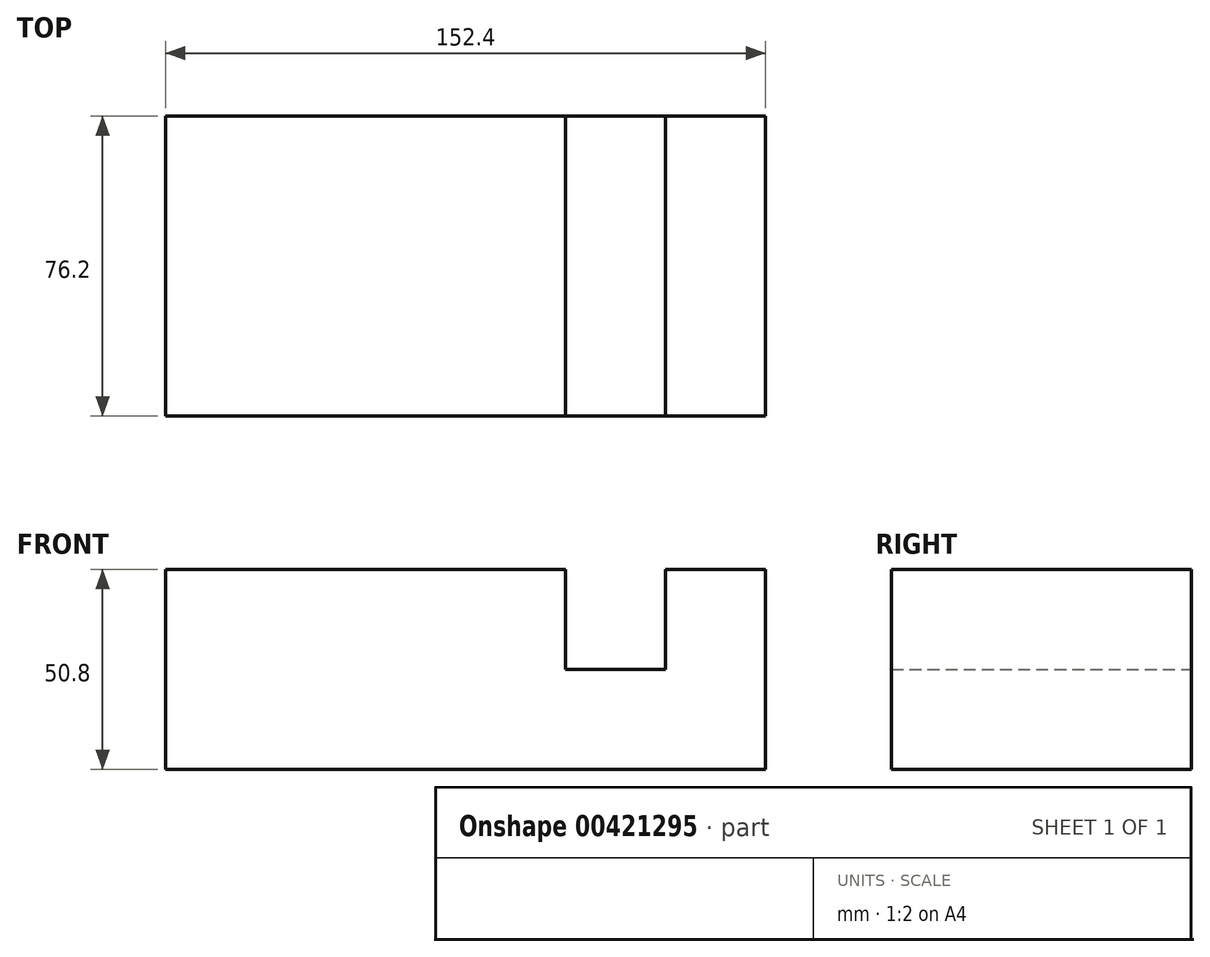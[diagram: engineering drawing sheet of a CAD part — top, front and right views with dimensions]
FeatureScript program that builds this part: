
annotation { "Feature Type Name" : "Feature", "Feature Type Description" : "" }
export const myFeature = defineFeature(function(context is Context, id is Id, definition is map)
    precondition{}
    {
        {
            var Q0;
            Q0=qCreatedBy(makeId("Front.planeOp"),FACE);
            var sketch = newSketch(context, id + "F0", { "sketchPlane" : qUnion([Q0])});
            skLineSegment(sketch, "E0", {"start": v(0, 0) * mm, "end": v(152.4, 0) * mm});
            skLineSegment(sketch, "E1", {"start": v(0, 0) * mm, "end": v(0, 50.8) * mm});
            skLineSegment(sketch, "E2", {"start": v(0, 50.8) * mm, "end": v(101.6, 50.8) * mm});
            skLineSegment(sketch, "E3", {"start": v(101.6, 50.8) * mm, "end": v(101.6, 25.4) * mm});
            skLineSegment(sketch, "E4", {"start": v(101.6, 25.4) * mm, "end": v(127, 25.4) * mm});
            skLineSegment(sketch, "E5", {"start": v(127, 25.4) * mm, "end": v(127, 50.8) * mm});
            skLineSegment(sketch, "E6", {"start": v(127, 50.8) * mm, "end": v(152.4, 50.8) * mm});
            skLineSegment(sketch, "E7", {"start": v(152.4, 50.8) * mm, "end": v(152.4, 0) * mm});
            skSolve(sketch);
        }
        {
            var Q0;
            Q0=makeQuery(id+"F0.imprint","IMPRINT",FACE,{"disambiguationData":[TD([[makeQuery(id+"F0.imprint","IMPRINT",EDGE,{"derivedFrom":sQuery(id+"F0.wireOp",EDGE,"E0")}),1.0]])]});
            extrude(context, id + "F1", {"entities" : qUnion([Q0]), "depth" : 76.2 * mm});
        }
    });
